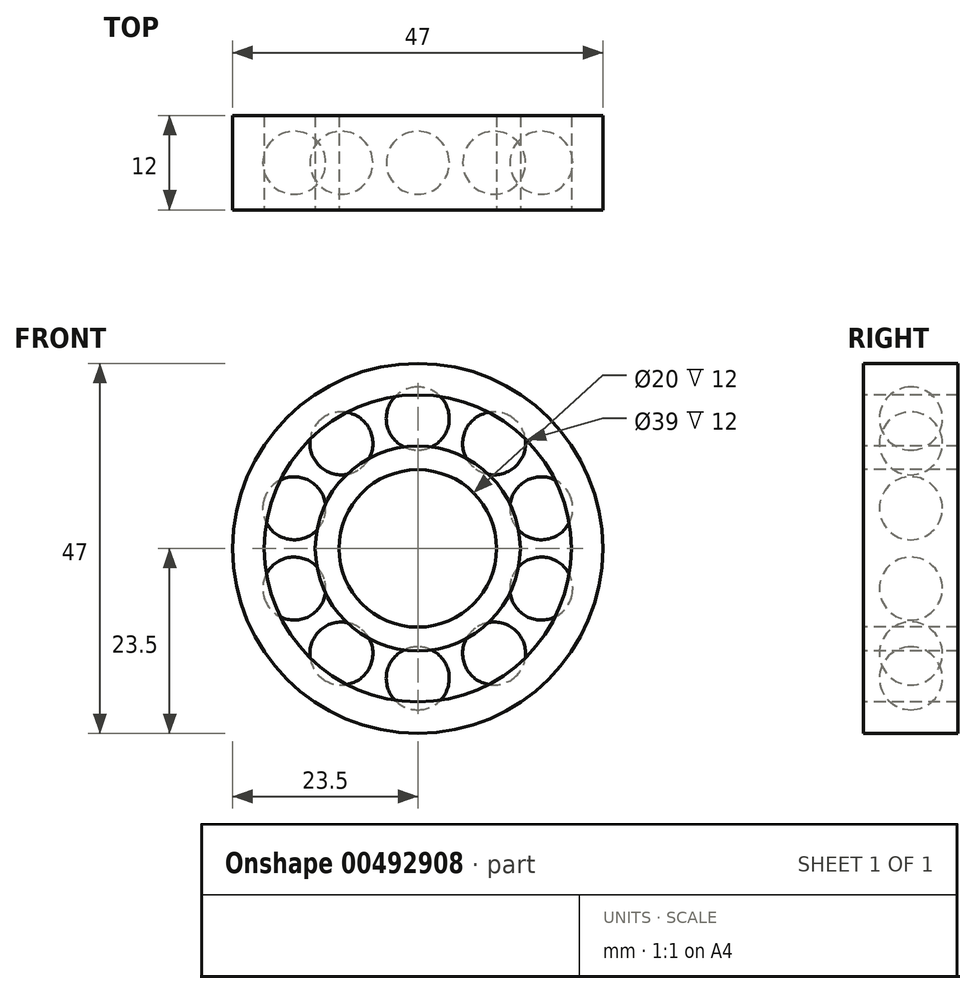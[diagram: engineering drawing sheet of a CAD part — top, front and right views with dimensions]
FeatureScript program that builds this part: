
annotation { "Feature Type Name" : "Feature", "Feature Type Description" : "" }
export const myFeature = defineFeature(function(context is Context, id is Id, definition is map)
    precondition{}
    {
        {
            var Q0;
            Q0=qCreatedBy(makeId("Front.planeOp"),FACE);
            var sketch = newSketch(context, id + "F0", { "sketchPlane" : qUnion([Q0])});
            skCircle(sketch, "E0", {"center": v(0, 0) * mm, "radius": 10 * mm});
            skCircle(sketch, "E1", {"center": v(0, 0) * mm, "radius": 13.02 * mm});
            skCircle(sketch, "E2", {"center": v(0, 0) * mm, "radius": 19.5 * mm});
            skCircle(sketch, "E3", {"center": v(0, 0) * mm, "radius": 23.5 * mm});
            skSolve(sketch);
        }
        {
            var Q0;
            Q0=makeQuery(id+"F0.imprint","IMPRINT",FACE,{"disambiguationData":[TD([[makeQuery(id+"F0.imprint","IMPRINT",EDGE,{"derivedFrom":sQuery(id+"F0.wireOp",EDGE,"E2")}),-1.0]])]});
            extrude(context, id + "F1", {"entities" : qUnion([Q0]), "oppositeDirection" : true, "depth" : 12 * mm});
        }
        {
            var Q0;
            Q0=makeQuery(id+"F0.imprint","IMPRINT",FACE,{"disambiguationData":[TD([[makeQuery(id+"F0.imprint","IMPRINT",EDGE,{"derivedFrom":sQuery(id+"F0.wireOp",EDGE,"E0")}),-1.0]])]});
            extrude(context, id + "F2", {"entities" : qUnion([Q0]), "oppositeDirection" : true, "depth" : 12 * mm});
        }
        {
            var Q0;
            Q0=qCreatedBy(makeId("Front.planeOp"),FACE);
            cPlane(context, id + "F3", {"entities" : qUnion([Q0]), "cplaneType" : CPlaneType.OFFSET, "offset" : 6 * mm, "oppositeDirection" : true, "width" : 150 * mm, "height" : 150 * mm});
        }
        {
            var Q0;
            Q0=qCreatedBy(id+"F3.planeOp",FACE);
            var sketch = newSketch(context, id + "F4", { "sketchPlane" : qUnion([Q0])});
            skArc(sketch, "E4", {"start": v(0, 12.5) * mm, "mid": v(4, 16.5) * mm, "end": v(0, 20.5) * mm});
            skLineSegment(sketch, "E5", {"start": v(0, 20.5) * mm, "end": v(0, 12.5) * mm});
            skPoint(sketch, "E6.orphan", {"position": v(0, 24.84) * mm});
            skSolve(sketch);
        }
        {
            var Q0;
            Q0=qCreatedBy(makeId("Right.planeOp"),FACE);
            var sketch = newSketch(context, id + "F5", { "sketchPlane" : qUnion([Q0])});
            skLineSegment(sketch, "E7", {"start": v(-30.82, 0) * mm, "end": v(47.23, 0) * mm, "construction": true});
            skSolve(sketch);
        }
        {
            var Q0;
            Q0 = qSketchRegion(id + "F4", true);
            var Q1;
            Q1=sQuery(id+"F4.wireOp",EDGE,"E5");
            revolve(context, id + "F6", {"surfaceOperationType" : NewSurfaceOperationType.NEW, "entities" : qUnion([Q0]), "axis" : qUnion([Q1]), "revolveType" : RevolveType.FULL});
        }
        {
            var Q0;
            Q0=makeQuery(id+"F6.opRevolve","SWEPT_BODY",BODY,{"disambiguationData":[OSD([sQuery(id+"F4.wireOp",EDGE,"E4"),sQuery(id+"F4.wireOp",EDGE,"E5")])]});
            var Q1;
            Q1=sQuery(id+"F5.wireOp",EDGE,"E7");
            circularPattern(context, id + "F7", {"entities" : qUnion([Q0]), "axis" : qUnion([Q1]), "angle" : 360 * degree, "instanceCount" : 10, "equalSpace" : true, "computeTransformsWithoutBuiltin" : true});
        }
    });
